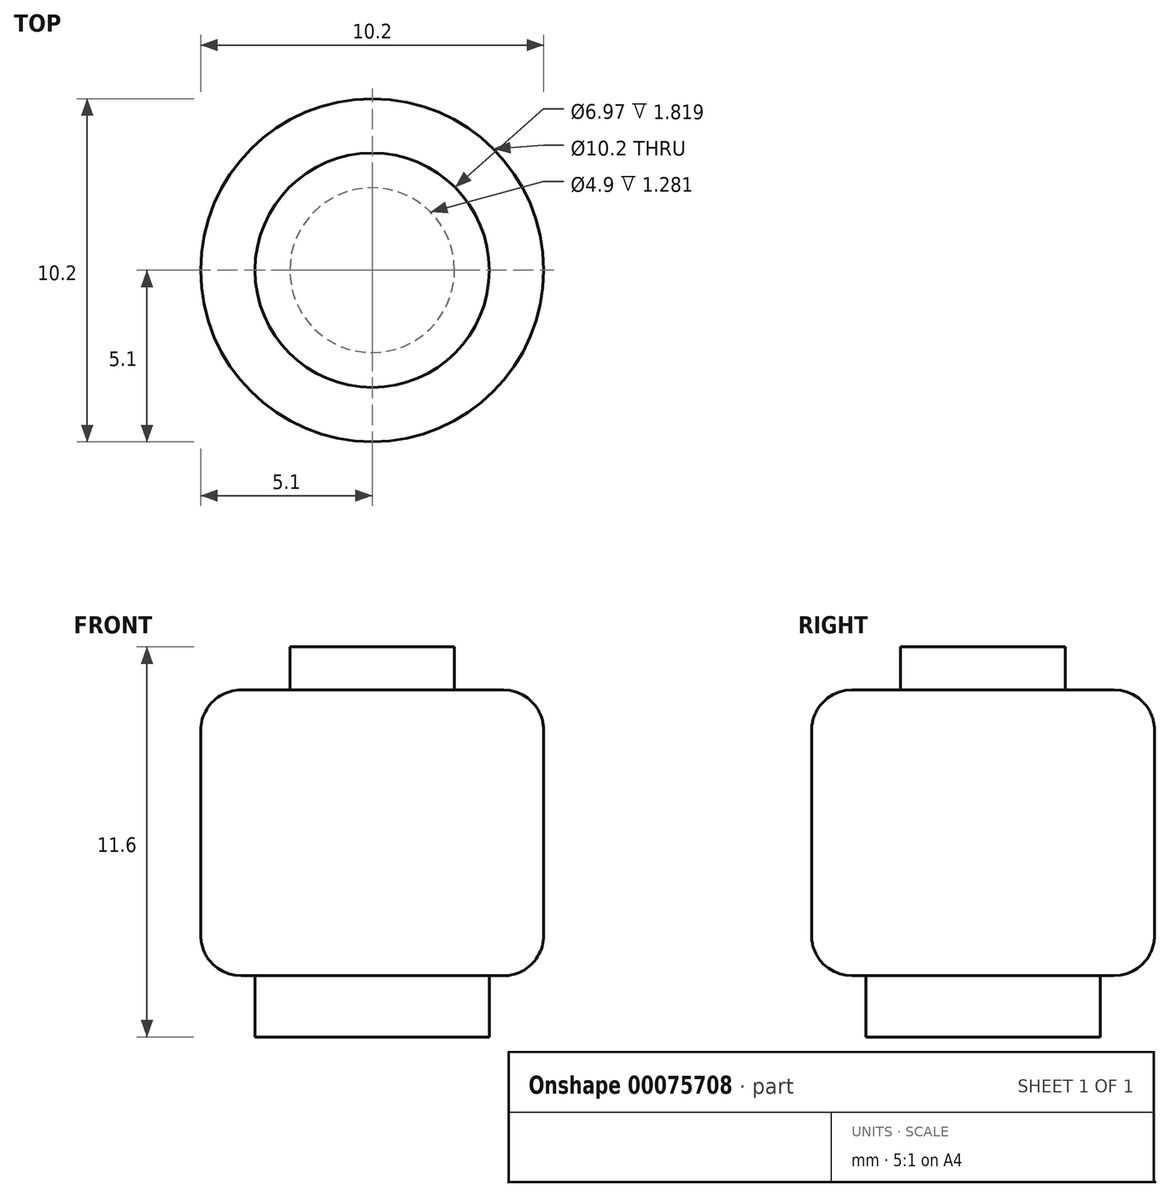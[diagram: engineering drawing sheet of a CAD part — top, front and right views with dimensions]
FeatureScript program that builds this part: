
annotation { "Feature Type Name" : "Feature", "Feature Type Description" : "" }
export const myFeature = defineFeature(function(context is Context, id is Id, definition is map)
    precondition{}
    {
        {
            var Q0;
            Q0=qCreatedBy(makeId("Front.planeOp"),FACE);
            var sketch = newSketch(context, id + "F0", { "sketchPlane" : qUnion([Q0])});
            skLineSegment(sketch, "E0", {"start": v(0, 0) * mm, "end": v(0, 11.6) * mm, "construction": true});
            skLineSegment(sketch, "E1", {"start": v(2.45, 11.6) * mm, "end": v(0, 11.6) * mm});
            skLineSegment(sketch, "E2", {"start": v(2.45, 10.32) * mm, "end": v(2.45, 11.6) * mm});
            skLineSegment(sketch, "E3", {"start": v(5.1, 10.32) * mm, "end": v(2.45, 10.32) * mm});
            skLineSegment(sketch, "E4", {"start": v(5.1, 1.82) * mm, "end": v(5.1, 10.32) * mm});
            skLineSegment(sketch, "E5", {"start": v(3.48, 1.82) * mm, "end": v(5.1, 1.82) * mm});
            skLineSegment(sketch, "E6", {"start": v(3.48, 0) * mm, "end": v(3.48, 1.82) * mm});
            skLineSegment(sketch, "E7", {"start": v(0, 0) * mm, "end": v(3.48, 0) * mm});
            skSolve(sketch);
        }
        {
            var Q0;
            Q0 = qSketchRegion(id + "F0", true);
            var Q1;
            Q1 = qBodyType(qCreatedBy(id + "F0" ,EDGE), BodyType.WIRE);
            var Q2;
            Q2=sQuery(id+"F0.wireOp",EDGE,"E0");
            revolve(context, id + "F1", {"bodyType" : ToolBodyType.SURFACE, "operationType" : NewBodyOperationType.ADD, "entities" : qUnion([Q0]), "surfaceEntities" : qUnion([Q1]), "axis" : qUnion([Q2]), "revolveType" : RevolveType.ONE_DIRECTION, "angle" : 360 * degree});
        }
        {
            var Q0;
            Q0=makeQuery(id+"F1.opRevolve","SWEPT_FACE",FACE,{"disambiguationData":[OSD([sQuery(id+"F0.wireOp",EDGE,"E4")])]});
            fillet(context, id + "F2", {"entities" : qUnion([Q0]), "radius" : 1.2 * mm, "tangentPropagation" : true, "allowEdgeOverflow" : false});
        }
    });
